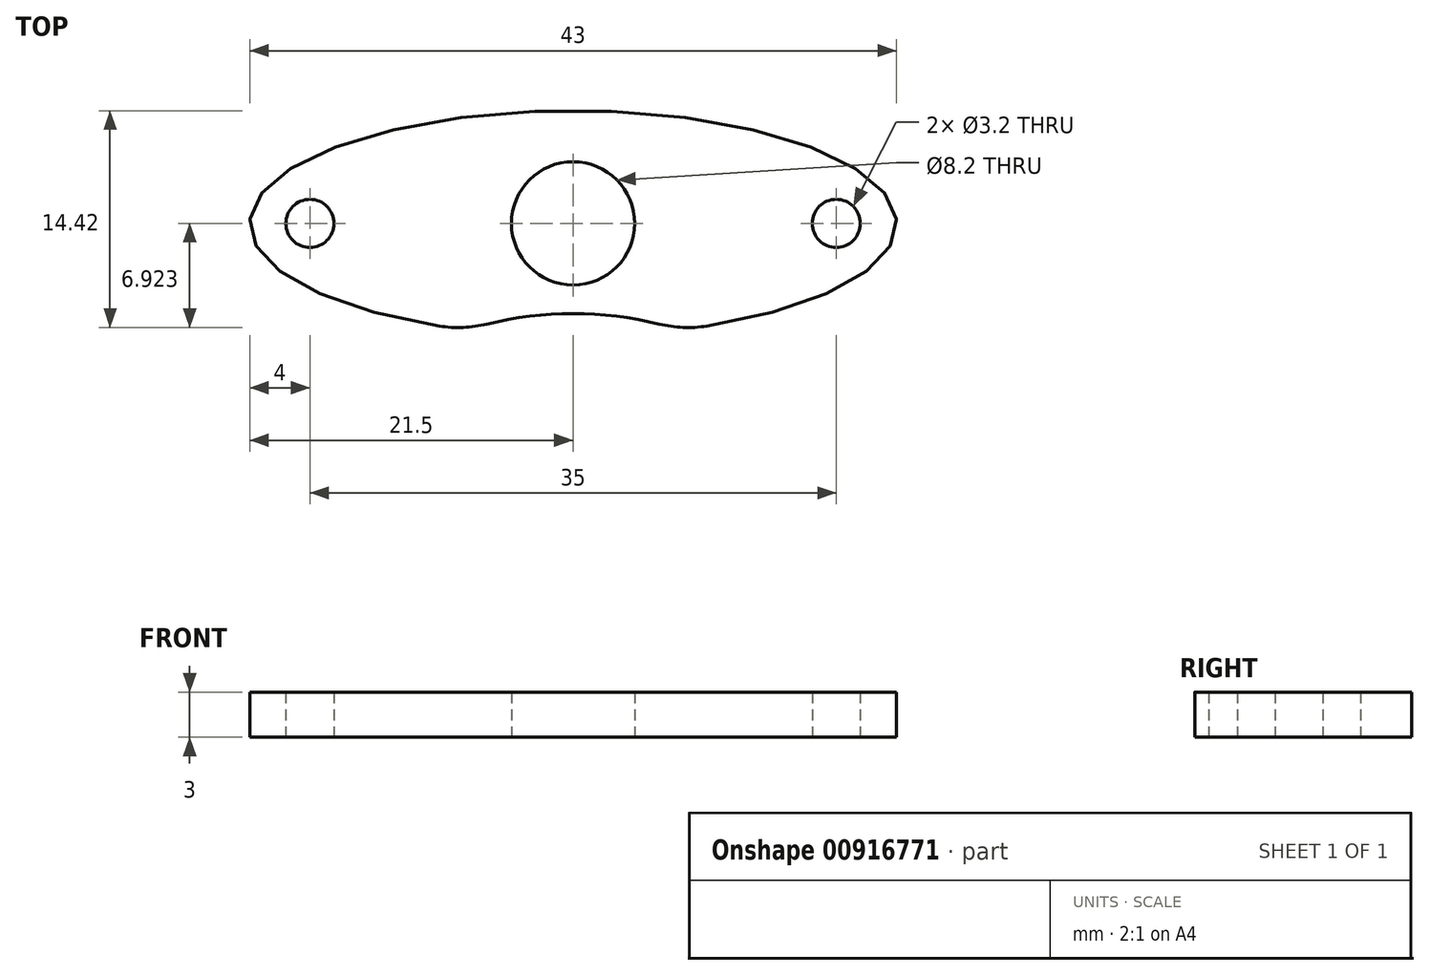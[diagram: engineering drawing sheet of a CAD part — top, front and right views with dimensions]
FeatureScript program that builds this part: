
annotation { "Feature Type Name" : "Feature", "Feature Type Description" : "" }
export const myFeature = defineFeature(function(context is Context, id is Id, definition is map)
    precondition{}
    {
        {
            var Q0;
            Q0=qCreatedBy(makeId("Top.planeOp"),FACE);
            var sketch = newSketch(context, id + "F0", { "sketchPlane" : qUnion([Q0])});
            skCircle(sketch, "E0", {"center": v(17.5, -0.29) * mm, "radius": 1.6 * mm});
            skArc(sketch, "E1", {"start": v(5.73, -6.98) * mm, "mid": v(0, -6.29) * mm, "end": v(-5.73, -6.98) * mm});
            skArc(sketch, "E2", {"start": v(5.73, -6.98) * mm, "mid": v(7.3, -7.2) * mm, "end": v(8.9, -7.11) * mm});
            skArc(sketch, "E3", {"start": v(-8.9, -7.11) * mm, "mid": v(-7.3, -7.2) * mm, "end": v(-5.73, -6.98) * mm});
            skCircle(sketch, "E4", {"center": v(-17.5, -0.29) * mm, "radius": 1.6 * mm});
            skEllipticalArc(sketch, "E5", {});
            skCircle(sketch, "E6", {"center": v(0, -0.29) * mm, "radius": 4.1 * mm});
            const initialGuessF0  = {"E5": [0, -0.00028677000000000005, -21.5, 0, 0.0215, 0.0075, 1.997442, 7.427336]};
            skSetInitialGuess(sketch, initialGuessF0);
            skSolve(sketch);
        }
        {
            var Q0;
            Q0=qSketchRegion(id+"F0",true);
            extrude(context, id + "F1", {"entities" : qUnion([Q0]), "depth" : 3 * mm, "offsetDistance" : 25 * mm});
        }
    });
